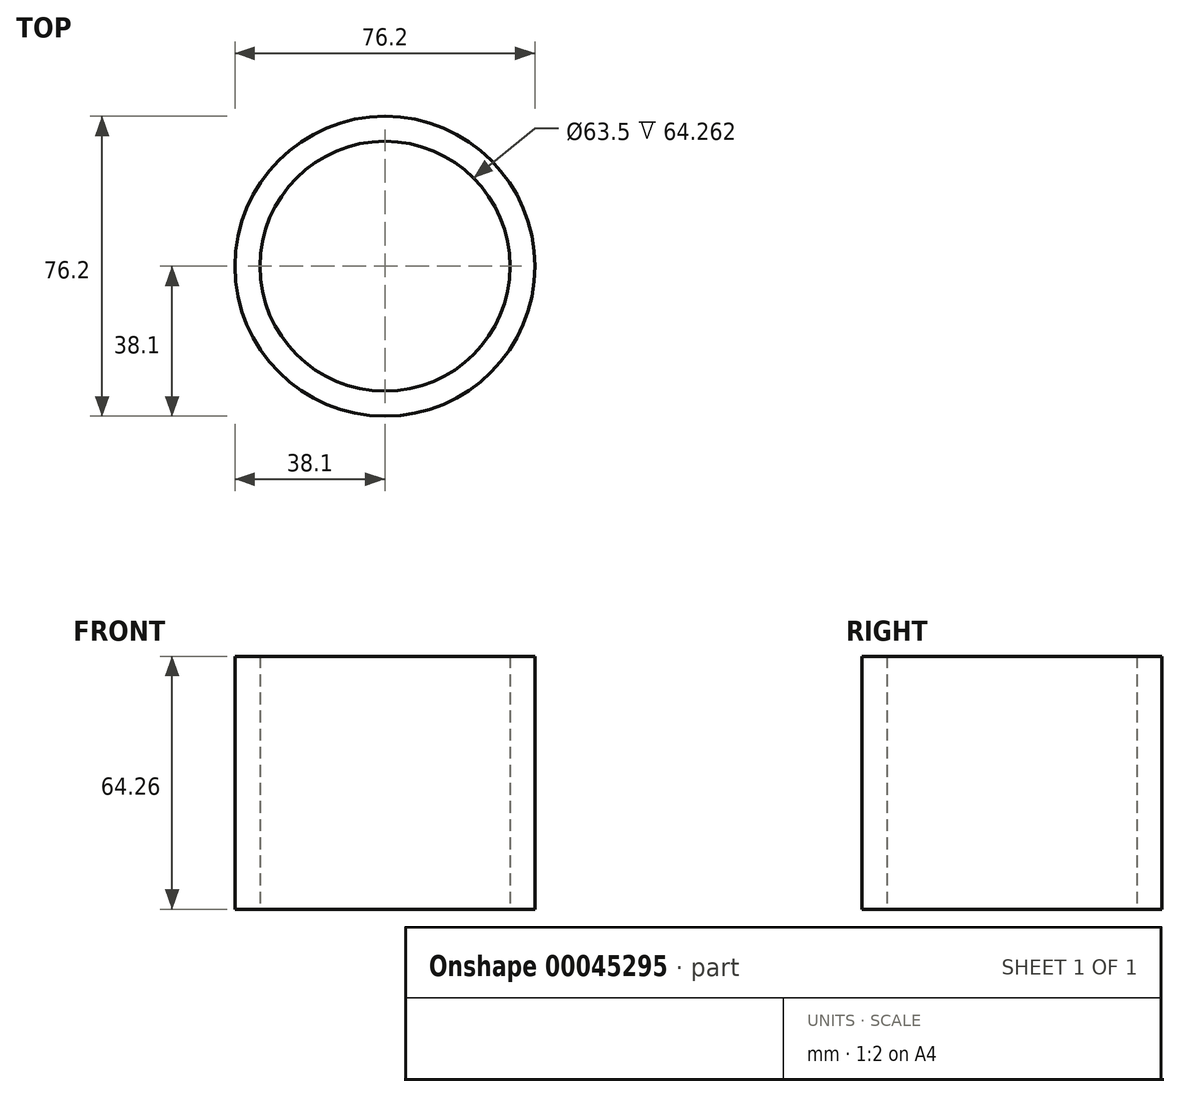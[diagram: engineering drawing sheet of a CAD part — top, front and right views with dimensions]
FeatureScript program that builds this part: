
annotation { "Feature Type Name" : "Feature", "Feature Type Description" : "" }
export const myFeature = defineFeature(function(context is Context, id is Id, definition is map)
    precondition{}
    {
        {
            var Q0;
            Q0=qCreatedBy(makeId("Top.planeOp"),FACE);
            var sketch = newSketch(context, id + "F0", { "sketchPlane" : qUnion([Q0])});
            skCircle(sketch, "E0", {"center": v(0, 0) * mm, "radius": 38.1 * mm});
            skCircle(sketch, "E1", {"center": v(0, 0) * mm, "radius": 31.75 * mm});
            skSolve(sketch);
        }
        {
            var Q0;
            Q0=makeQuery(id+"F0.imprint","IMPRINT",FACE,{"disambiguationData":[TD([[makeQuery(id+"F0.imprint","IMPRINT",EDGE,{"derivedFrom":sQuery(id+"F0.wireOp",EDGE,"E0")}),1.0]])]});
            extrude(context, id + "F1", {"entities" : qUnion([Q0]), "depth" : 64.26 * mm});
        }
    });
